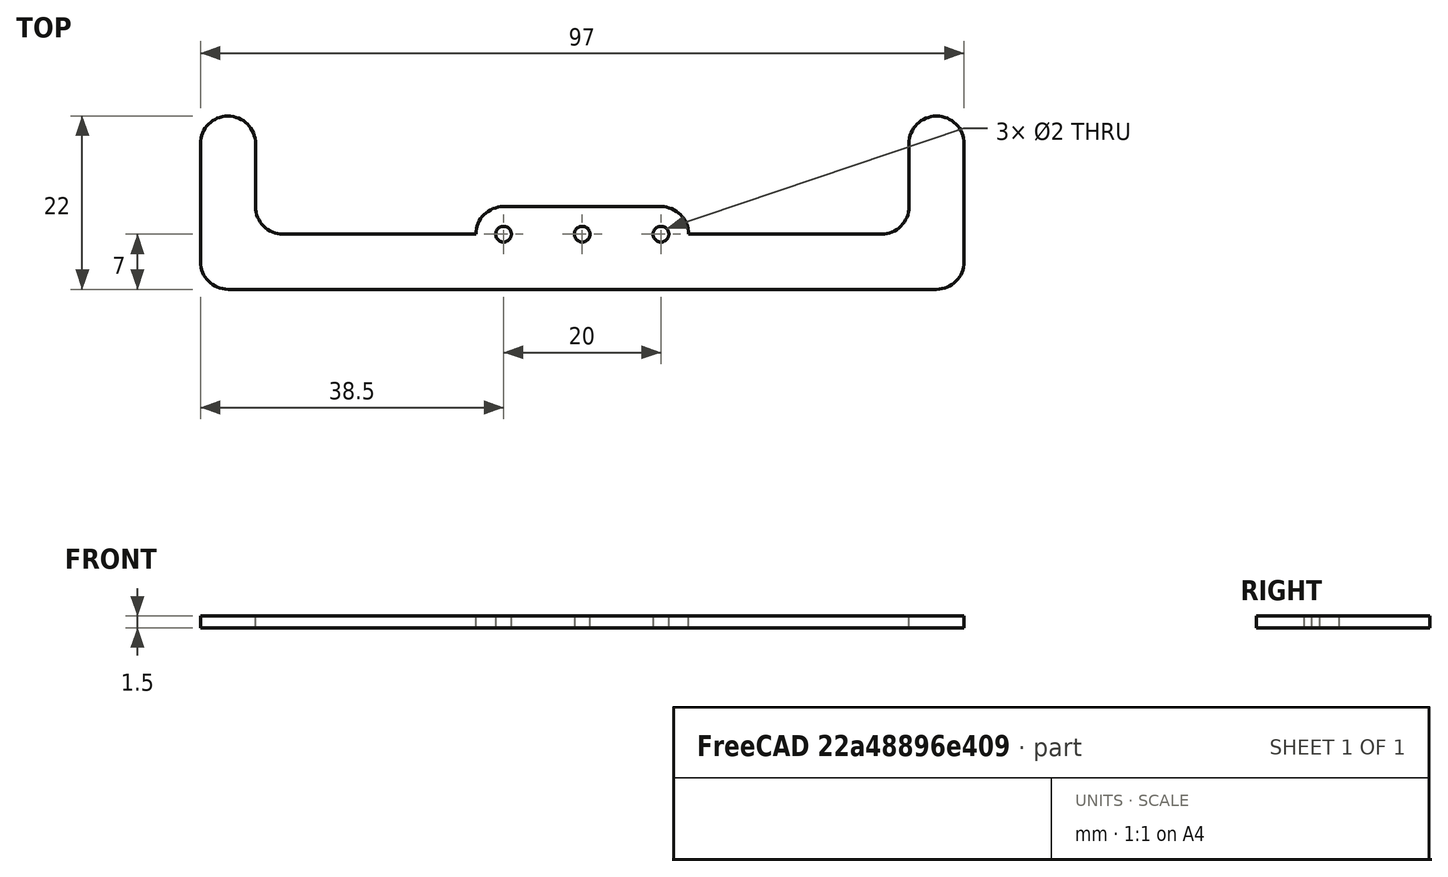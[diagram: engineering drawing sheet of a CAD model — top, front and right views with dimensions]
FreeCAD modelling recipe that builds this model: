
FCSTD DOCUMENT  (FreeCAD 0.19R24276 (Git))
Label: ServoArm
License: All rights reserved
LicenseURL: http://en.wikipedia.org/wiki/All_rights_reserved
objects: Sketcher::SketchObject×1, Spreadsheet::Sheet×1, PartDesign::Pad×1, PartDesign::Body×1, Mesh::Feature×1
note: 4 computed .brp shape members not serialized (recipe doc carries the construction recipe); baked Part::Feature solids carry a one-line shape summary decoded from their .brp

FEATURE [Sketcher::SketchObject] Sketch
  FullyConstrained = true
  MapMode = 5
  Support = -> [XY_Plane]
  expr: Constraints[64] = <<data>>.armLength
  expr: Constraints[39] = <<data>>.armThickness
  expr: Constraints[60] = <<data>>.armThickness / 2
  expr: Constraints[48] = <<data>>.armThickness / 2
  expr: Constraints[16] = <<data>>.armHeight - <<data>>.armThickness
  expr: Constraints[44] = <<data>>.holeDia / 2
  expr: Constraints[52] = <<data>>.armThickness + <<data>>.armThickness / 2
  expr: Constraints[54] = <<data>>.armThickness / 2
  expr: Constraints[49] = <<data>>.armThickness / 2
  expr: Constraints[20] = <<data>>.armThickness / 2
  expr: Constraints[45] = <<data>>.holeDia / 2
  expr: Constraints[2] = <<data>>.armLength
  expr: Constraints[27] = <<data>>.armThickness / 2
  expr: Constraints[9] = <<data>>.armThickness / 2
  expr: Constraints[41] = <<data>>.armThickness + <<data>>.armThickness / 2
  expr: Constraints[14] = <<data>>.armThickness / 2
  expr: Constraints[55] = <<data>>.armThickness / 2
  expr: Constraints[50] = <<data>>.armThickness / 2
  expr: Constraints[18] = <<data>>.armThickness
  expr: Constraints[36] = <<data>>.armHeight - <<data>>.armThickness
  expr: Constraints[43] = <<data>>.holeDia / 2
  expr: Constraints[30] = <<data>>.armHeight
  expr: Constraints[32] = <<data>>.armThickness / 2
  expr: Constraints[61] = <<data>>.armThickness / 2
  expr: Constraints[23] = <<data>>.armLength
  expr: Constraints[19] = <<data>>.armThickness
  expr: Constraints[38] = <<data>>.armThickness / 2
  expr: Constraints[7] = <<data>>.armHeight
  sketch-geometry (20):
    g0: LineSegment StartX=0 StartY=-3.5 StartZ=0 EndX=-45 EndY=-3.5 EndZ=0
    g1: ArcOfCircle CenterX=-45 CenterY=0 CenterZ=0 NormalX=0 NormalY=0 NormalZ=1 AngleXU=0 Radius=3.5 StartAngle=3.14159 EndAngle=4.71239
    g2: LineSegment StartX=-48.5 StartY=0 StartZ=0 EndX=-48.5 EndY=15 EndZ=0
    g3: ArcOfCircle CenterX=-45 CenterY=15 CenterZ=0 NormalX=0 NormalY=0 NormalZ=1 AngleXU=0 Radius=3.5 StartAngle=5.34385e-06 EndAngle=3.1416
    g4: ArcOfCircle CenterX=-38 CenterY=7.00002 CenterZ=0 NormalX=0 NormalY=0 NormalZ=1 AngleXU=0 Radius=3.50002 StartAngle=3.14159 EndAngle=4.71238
    g5: LineSegment StartX=-41.5 StartY=15 StartZ=0 EndX=-41.5 EndY=7.00004 EndZ=0
    g6: LineSegment StartX=0 StartY=-3.5 StartZ=0 EndX=45 EndY=-3.5 EndZ=0
    g7: ArcOfCircle CenterX=45 CenterY=0 CenterZ=0 NormalX=0 NormalY=0 NormalZ=1 AngleXU=0 Radius=3.5 StartAngle=4.71239 EndAngle=6.28319
    g8: LineSegment StartX=48.5 StartY=0 StartZ=0 EndX=48.5 EndY=15 EndZ=0
    g9: ArcOfCircle CenterX=45 CenterY=15 CenterZ=0 NormalX=0 NormalY=0 NormalZ=1 AngleXU=0 Radius=3.5 StartAngle=2e-16 EndAngle=3.14159
    g10: LineSegment StartX=41.5 StartY=15 StartZ=0 EndX=41.5 EndY=7 EndZ=0
    g11: ArcOfCircle CenterX=38 CenterY=7 CenterZ=0 NormalX=0 NormalY=0 NormalZ=1 AngleXU=0 Radius=3.5 StartAngle=4.71239 EndAngle=6.28319
    g12: Circle CenterX=0 CenterY=3.5 CenterZ=0 NormalX=0 NormalY=0 NormalZ=1 AngleXU=0 Radius=1
    g13: Circle CenterX=-10 CenterY=3.5 CenterZ=0 NormalX=0 NormalY=0 NormalZ=1 AngleXU=0 Radius=1
    g14: Circle CenterX=10 CenterY=3.5 CenterZ=0 NormalX=0 NormalY=0 NormalZ=1 AngleXU=0 Radius=1
    g15: LineSegment StartX=-10 StartY=7 StartZ=0 EndX=10 EndY=7 EndZ=0
    g16: ArcOfCircle CenterX=-10 CenterY=3.5 CenterZ=0 NormalX=0 NormalY=0 NormalZ=1 AngleXU=0 Radius=3.5 StartAngle=1.5708 EndAngle=3.14159
    g17: LineSegment StartX=-38 StartY=3.5 StartZ=0 EndX=-13.5 EndY=3.5 EndZ=0
    g18: ArcOfCircle CenterX=10 CenterY=3.5 CenterZ=0 NormalX=0 NormalY=0 NormalZ=1 AngleXU=0 Radius=3.5 StartAngle=0 EndAngle=1.5708
    g19: LineSegment StartX=38 StartY=3.5 StartZ=0 EndX=13.5 EndY=3.5 EndZ=0
  constraints (67):
    c: PointOnObject(g0,g-2)
    c: Horizontal(g0)
    c: DistanceX(g0,g0) = 45
    c: PointOnObject(g1,g-1)
    c: PointOnObject(g1,g-1)
    c: Coincident(g2,g1)
    c: Vertical(g2)
    c: DistanceY(g1,g2) = 15
    c: Coincident(g3,g2)
    c: Radius(g3) = 3.5
    c: Coincident(g5,g3)
    c: Coincident(g5,g4)
    c: Vertical(g5)
    c: Coincident(g0,g1)
    c: Radius(g1) = 3.5
    c: Angle(g3) = 3.14159
    c: DistanceY(g4,g3) = 8
    c: Angle(g4) = 1.5708
    c: DistanceX(g2,g3) = 7
    c: DistanceY(g0,g4) = 7
    c: DistanceX(g4,g4) = 3.5
    c: Coincident(g6,g0)
    c: Horizontal(g6)
    c: DistanceX(g0,g6) = 45
    c: PointOnObject(g7,g-1)
    c: Coincident(g7,g6)
    c: PointOnObject(g7,g-1)
    c: DistanceX(g7,g7) = 3.5
    c: Coincident(g8,g7)
    c: Vertical(g8)
    c: DistanceY(g7,g8) = 15
    c: Coincident(g9,g8)
    c: Radius(g9) = 3.5
    c: Angle(g9) = 3.14159
    c: Coincident(g10,g9)
    c: Vertical(g10)
    c: DistanceY(g10,g9) = 8
    c: Coincident(g11,g10)
    c: Radius(g11) = 3.5
    c: DistanceY(g6,g11) = 7
    c: Angle(g11) = 1.5708
    c: DistanceY(g6,g10) = 10.5
    c: PointOnObject(g12,g-2)
    c: Radius(g12) = 1
    c: Radius(g13) = 1
    c: Radius(g14) = 1
    c: DistanceX(g13,g12) = 10
    c: DistanceX(g12,g14) = 10
    c: DistanceY(g-1,g13) = 3.5
    c: DistanceY(g-1,g12) = 3.5
    c: DistanceY(g-1,g14) = 3.5
    c: Horizontal(g15)
    c: DistanceY(g0,g15) = 10.5
    c: Coincident(g16,g15)
    c: DistanceX(g16,g15) = 3.5
    c: DistanceX(g16,g13) = 3.5
    c: Coincident(g17,g4)
    c: Coincident(g17,g16)
    c: Horizontal(g17)
    c: Coincident(g18,g15)
    c: DistanceX(g15,g18) = 3.5
    c: DistanceY(g18,g15) = 3.5
    c: Coincident(g19,g11)
    c: Coincident(g19,g18)
    c: DistanceX(g3,g0) = 45
    c: DistanceX(g16,g-1) = 10
    c: Coincident(g14,g18)
FEATURE [Spreadsheet::Sheet] Spreadsheet  label="data"
  cells = A4=armLength; B4(armLength)==45mm; A5=armHeight; B5(armHeight)==15mm; A6=armThickness; B6(armThickness)==7mm; A7=holeDia; B7(holeDia)==2mm; A8=holeSpacing; B8(holeSpacing)==20mm
FEATURE [PartDesign::Pad] Pad
  Direction = (1,1,1)
  Length = 1.5
  Length2 = 100
  Profile = -> Sketch
  Type = 0
FEATURE [PartDesign::Body] Body
  Group = -> [Sketch,Pad]
  Origin = -> Origin
  Tip = -> Pad
FEATURE [Mesh::Feature] SG90_Dual_Horn_R2_3  label="SG90_Dual_Horn_R2.3"
  Placement = pos=(0,0,-1) rot=(0,0,1;0rad)
